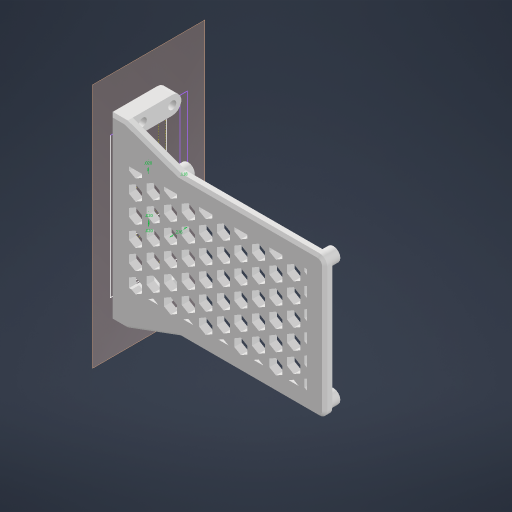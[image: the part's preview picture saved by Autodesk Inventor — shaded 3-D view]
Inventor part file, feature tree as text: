
AUTODESK INVENTOR PART (.ipt)
format: ipt  version: 2024 (Build 280153000, 153)  size: 1,030,144 bytes
history: native  units: in
note: dims shown in document units (in); Inventor stores cm internally (conversion verified against a paired STEP export)
features: reference x6, projected_geometry x6, sketch x5, other x5, extrude x4, plane x1, chamfer x1, fillet x1
ambient origin geometry x8: Origin, YZ Plane, XZ Plane, XY Plane, X Axis, Y Axis, Z Axis, Center Point
bodies: Solid1 (feature_tree)
feature tree (29):
  extrude  "Extrusion1"  Depth=0.2165in
  extrude  "Extrusion3"  Depth=0.2165in
  sketch  "Sketch4"  dims[d4=0.0866in d5=0.0866in]
  plane  "Work Plane1"
  extrude  "Extrusion4"  Depth=0.0866in
  extrude  "Extrusion5"  Depth=0.2756in
  chamfer  "Chamfer1"  Distance=0.1575in
  fillet  "Fillet1"  Radius=0.2756in
  sketch  "Sketch1"  dims[d0=0.2165in d1=0.2165in]
  reference  "Reference1"
  sketch  "Sketch2"  dims[d2=0.2165in d3=0.2165in]
  projected_geometry  "Projected Loop1"
  projected_geometry  "Projected Loop2"
  projected_geometry  "Projected Loop3"
  projected_geometry  "Projected Loop4"
  reference  "Reference2"
  reference  "Reference3"
  reference  "Reference4"
  reference  "Reference5"
  projected_geometry  "Projected Loop6"
  sketch  "Sketch5"  dims[d6=0.0866in d7=0.0866in d8=0.1575in d9=0.0in d16=0.2756in]
  reference  "Reference6"
  sketch  "Sketch6"  dims[d17=0.2756in d18=2.0079in d19=1.9685in d21=0.315in d22=0.7874in d24=0.315in d27=0.7874in d29=0.315in d30=0.3937in d32=1.0in d34=0.7874in d36=0.315in d37=0.3937in d39=1.0in d41=2.3622in d43=0.5512in d44=0.3937in d46=1.0in d48=0.3937in d50=0.2756in d51=1.1811in d53=0.5512in d54=0.3937in d56=1.0in d58=0.1181in d59=0.0in d60=0.0197in d61=0.0197in d62=0.0197in d63=0.0197in d64=0.2756in d65=0.1181in d66=0.0787in d67=0.0787in d68=0.0787in d69=0.0787in d70=0.2362in d71=0.0in d72=0.1378in d73=0.0in d74=0.0394in d75=0.125in d76=45.0deg d77=0.125in]
  projected_geometry  "Projected Loop7"
  other  "<userpath>\Desktop\SeniorDesign\Head_V3\RaspberryPi_Encloser.iam"
  other  "RaspberryPi_Encloser.iam"
  other  "RaspberryPi4:1"
  other  "RaspberryPi_IO_Shield:1"
  other  "Assembly3"
